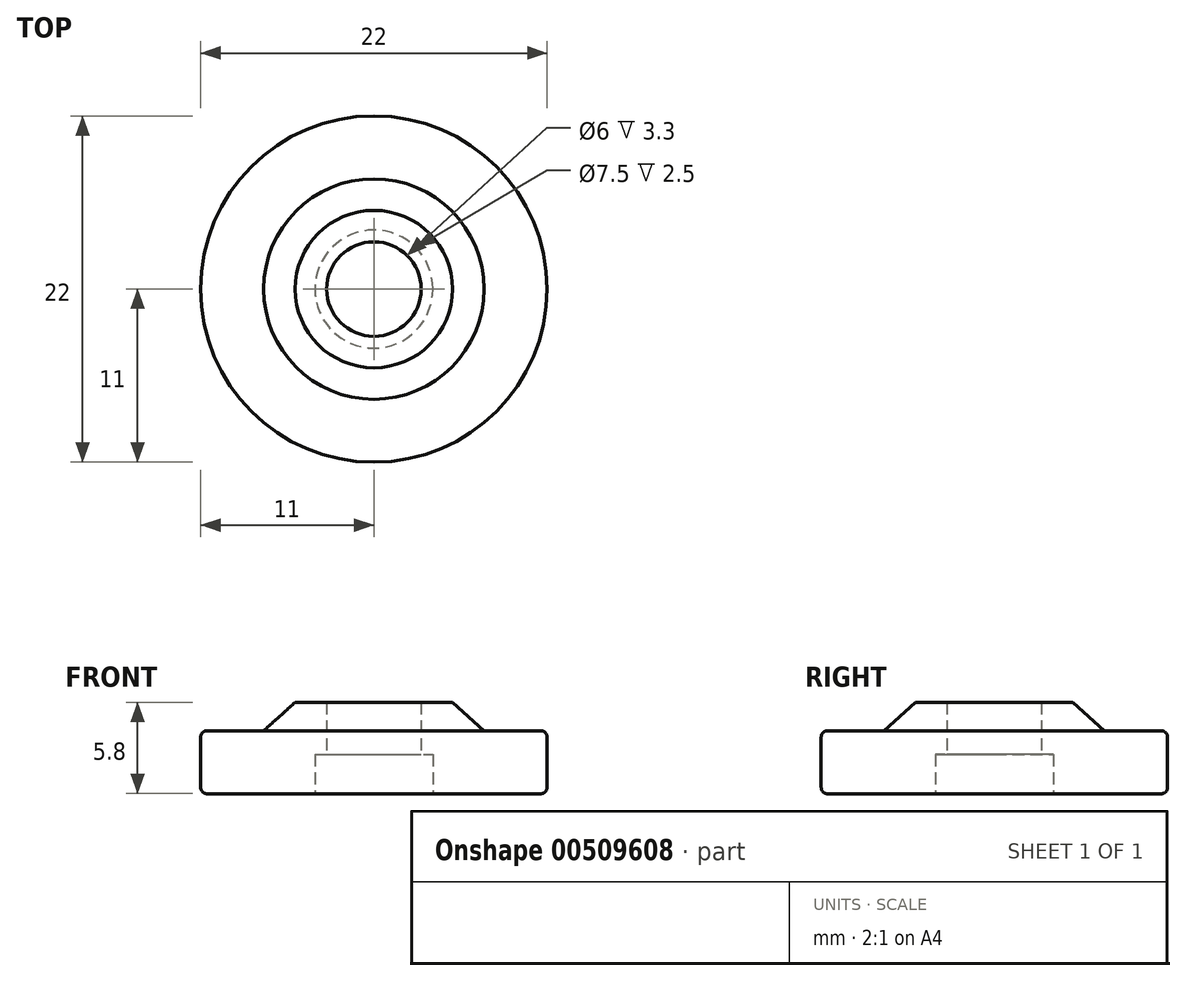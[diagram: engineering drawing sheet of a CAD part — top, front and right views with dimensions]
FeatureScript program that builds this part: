
annotation { "Feature Type Name" : "Feature", "Feature Type Description" : "" }
export const myFeature = defineFeature(function(context is Context, id is Id, definition is map)
    precondition{}
    {
        {
            var Q0;
            Q0=qCreatedBy(makeId("Front.planeOp"),FACE);
            var sketch = newSketch(context, id + "F0", { "sketchPlane" : qUnion([Q0])});
            skLineSegment(sketch, "E0", {"start": v(0, 27.32) * mm, "end": v(-11, 27.32) * mm});
            skLineSegment(sketch, "E1", {"start": v(-11, 27.32) * mm, "end": v(-11, 40.24) * mm});
            skPoint(sketch, "E2", {"position": v(-11, 29.32) * mm});
            skLineSegment(sketch, "E3", {"start": v(0, 27.32) * mm, "end": v(0, 33.12) * mm});
            skLineSegment(sketch, "E4", {"start": v(0, 33.12) * mm, "end": v(-5, 33.12) * mm});
            skLineSegment(sketch, "E5", {"start": v(-11, 31.32) * mm, "end": v(-7, 31.32) * mm});
            skLineSegment(sketch, "E6", {"start": v(-7, 31.32) * mm, "end": v(-5, 33.12) * mm});
            skLineSegment(sketch, "E7", {"start": v(-3.75, 27.32) * mm, "end": v(-3.75, 29.82) * mm});
            skLineSegment(sketch, "E8", {"start": v(-3.75, 29.82) * mm, "end": v(-3, 29.82) * mm});
            skLineSegment(sketch, "E9", {"start": v(-3, 29.82) * mm, "end": v(-3, 33.12) * mm});
            skSolve(sketch);
        }
        {
            var Q0;
            {var subQ6=sQuery(id+"F0.wireOp",EDGE,"E5");Q0=makeQuery(id+"F0.imprint","IMPRINT",FACE,{"disambiguationData":[TD([[makeQuery(id+"F0.imprint","IMPRINT",EDGE,{"derivedFrom":subQ6}),-1.0]])]});}
            var Q1;
            Q1=sQuery(id+"F0.wireOp",EDGE,"E3");
            revolve(context, id + "F1", {"entities" : qUnion([Q0]), "axis" : qUnion([Q1]), "revolveType" : RevolveType.FULL});
        }
        {
            var Q0;
            Q0=makeQuery(id+"F1.opRevolve","SWEPT_EDGE",EDGE,{"disambiguationData":[OSD([sQuery(id+"F0.wireOp",EDGE,"E1"),sQuery(id+"F0.wireOp",EDGE,"E5")])]});
            var Q1;
            Q1=makeQuery(id+"F1.opRevolve","SWEPT_EDGE",EDGE,{"disambiguationData":[OSD([sQuery(id+"F0.wireOp",EDGE,"E0"),sQuery(id+"F0.wireOp",EDGE,"E1")])]});
            fillet(context, id + "F2", {"entities" : qUnion([Q0, Q1]), "radius" : .4 * mm, "tangentPropagation" : true, "allowEdgeOverflow" : false});
        }
    });
